# Revit family: Univers-IP30-empty-Surface_mounted-NoHosted-CH-en
name_source: partatom
category: Electrical Equipment
units: mm (PartAtom-declared; Revit-internal decimal feet)

## family parameters
Always vertical = Yes
Cut with Voids When Loaded = No
Panel Configuration = Two Columns, Circuits Across
Part Type = Panelboard
Room Calculation Point = No
Round Connector Dimension = Use Diameter
Shared = No
Work Plane-Based = Yes

## types (20) — shared parameters
Default Elevation = 1219 mm
EF000007 - Colour = EV000202 - White
EF000049 - Depth = 161 mm  [stored 0.528215 ft]
EF000116 - RAL-number = 9010
EF000118 - With mounting plate = No
EF000339 - Type of cover = EV000494 - None
EF001062 - EMC-version = No
EF001088 - Extension possible = No
EF001134 - DIN-rail = No
EF001596 - Material housing = EV000179 - Steel
EF004462 - Type of closure = EV000154 - Other
EF005474 - Degree of protection (IP) = EV006410 - IP30
EF006244 - Transparent cover/door = No
EF006306 - With lock = No
EF015776 - Earthing terminal block = No
EF015777 - Neutral terminal block = No
EF015941 - Signal passing door = No
HG000002 - With door or cover = No
HG000003 - Range = Univers
HG000005 - Thickness = 3 mm  [stored 0.00984252 ft]
HG000006 - Flush mounted = No
HG000009 - Double swing door = No
HG000010 - Asymmetric doors = No
HG000011 - Empty rows from bottom = No
Manufacturer = Hager
Type Comments = Univers
zero-valued in all types: EF000266 - Number of rows, EF002950 - Width in number of modular spacings, HG000001 - Number of columns, HG000007 - Number of empty columns, HG000008 - Number of empty rows

## per-type parameters (varying)
| type | EF000003 - Mounting method | EF000008 - Width | EF000040 - Height | EF000218 - Built-in depth | EF000332 - Built-in height | EF000846 - Built-in width | EF001131 - Internal depth | EF009212 - Cover model | HG000004 - Manufacturer reference | Model |
| Surface mounted IP30 W1050 H1100 D161 0 Modular spacings - FWB74D1 | EV001247 - Surface mounted/recessed mounted | 1050 mm | 1100 mm | 161 mm  [stored 0.528215 ft] | 1100 mm | 1050 mm | 156 mm  [stored 0.511811 ft] | EV009916 - With notch | FWB74D1 | FWB74D1 |
| Surface mounted IP30 W1050 H500 D161 0 Modular spacings - FWB34D1 | EV001247 - Surface mounted/recessed mounted | 1050 mm | 500 mm  [stored 1.64042 ft] | 161 mm  [stored 0.528215 ft] | 500 mm  [stored 1.64042 ft] | 1050 mm | 156 mm  [stored 0.511811 ft] | EV009916 - With notch | FWB34D1 | FWB34D1 |
| Surface mounted IP30 W1050 H650 D161 0 Modular spacings - FWB44D1 | EV001247 - Surface mounted/recessed mounted | 1050 mm | 650 mm  [stored 2.13255 ft] | 161 mm  [stored 0.528215 ft] | 650 mm  [stored 2.13255 ft] | 1050 mm | 160 mm  [stored 0.524934 ft] | EV000116 - Closed | FWB44D1 | FWB44D1 |
| Surface mounted IP30 W1050 H800 D161 0 Modular spacings - FWB54D1 | EV001247 - Surface mounted/recessed mounted | 1050 mm | 800 mm  [stored 2.62467 ft] | 161 mm  [stored 0.528215 ft] | 800 mm  [stored 2.62467 ft] | 1050 mm | 160 mm  [stored 0.524934 ft] | EV009916 - With notch | FWB54D1 | FWB54D1 |
| Surface mounted IP30 W1050 H950 D161 0 Modular spacings - FWB64D1 | EV001247 - Surface mounted/recessed mounted | 1050 mm | 950 mm  [stored 3.1168 ft] | 161 mm  [stored 0.528215 ft] | 950 mm  [stored 3.1168 ft] | 1050 mm | 160 mm  [stored 0.524934 ft] | EV009916 - With notch | FWB64D1 | FWB64D1 |
| Surface mounted IP30 W300 H1100 D161 0 Modular spacings - FWB71D1 | EV001247 - Surface mounted/recessed mounted | 300 mm | 1100 mm | 161 mm  [stored 0.528215 ft] | 1100 mm | 300 mm | 156 mm  [stored 0.511811 ft] | EV009916 - With notch | FWB71D1 | FWB71D1 |
| Surface mounted IP30 W300 H1250 D161 0 Modular spacings - FWB81D1 | EV000384 - Surface mounted (plaster) | 300 mm | 1250 mm  [stored 4.10105 ft] | 0 mm  [stored 0 ft] | 0 mm  [stored 0 ft] | 0 mm  [stored 0 ft] | 160 mm  [stored 0.524934 ft] | EV009916 - With notch | FWB81D1 | FWB81D1 |
| Surface mounted IP30 W300 H500 D161 0 Modular spacings - FWB31D1 | EV001247 - Surface mounted/recessed mounted | 300 mm | 500 mm  [stored 1.64042 ft] | 161 mm  [stored 0.528215 ft] | 500 mm  [stored 1.64042 ft] | 300 mm | 156 mm  [stored 0.511811 ft] | EV009916 - With notch | FWB31D1 | FWB31D1 |
| Surface mounted IP30 W300 H650 D161 0 Modular spacings - FWB41D1 | EV001247 - Surface mounted/recessed mounted | 300 mm | 650 mm  [stored 2.13255 ft] | 161 mm  [stored 0.528215 ft] | 650 mm  [stored 2.13255 ft] | 300 mm | 160 mm  [stored 0.524934 ft] | EV000116 - Closed | FWB41D1 | FWB41D1 |
| Surface mounted IP30 W300 H800 D161 0 Modular spacings - FWB51D1 | EV001247 - Surface mounted/recessed mounted | 300 mm | 800 mm  [stored 2.62467 ft] | 161 mm  [stored 0.528215 ft] | 800 mm  [stored 2.62467 ft] | 300 mm | 156 mm  [stored 0.511811 ft] | EV009916 - With notch | FWB51D1 | FWB51D1 |
| Surface mounted IP30 W300 H950 D161 0 Modular spacings - FWB61D1 | EV001247 - Surface mounted/recessed mounted | 300 mm | 950 mm  [stored 3.1168 ft] | 161 mm  [stored 0.528215 ft] | 950 mm  [stored 3.1168 ft] | 300 mm | 156 mm  [stored 0.511811 ft] | EV009916 - With notch | FWB61D1 | FWB61D1 |
| Surface mounted IP30 W550 H1100 D161 0 Modular spacings - FWB72D1 | EV001247 - Surface mounted/recessed mounted | 550 mm | 1100 mm | 161 mm  [stored 0.528215 ft] | 1100 mm | 550 mm | 156 mm  [stored 0.511811 ft] | EV009916 - With notch | FWB72D1 | FWB72D1 |
| Surface mounted IP30 W550 H500 D161 0 Modular spacings - FWB32D1 | EV001247 - Surface mounted/recessed mounted | 550 mm | 500 mm  [stored 1.64042 ft] | 161 mm  [stored 0.528215 ft] | 500 mm  [stored 1.64042 ft] | 550 mm | 156 mm  [stored 0.511811 ft] | EV009916 - With notch | FWB32D1 | FWB32D1 |
| Surface mounted IP30 W550 H650 D161 0 Modular spacings - FWB42D1 | EV001247 - Surface mounted/recessed mounted | 550 mm | 650 mm  [stored 2.13255 ft] | 161 mm  [stored 0.528215 ft] | 650 mm  [stored 2.13255 ft] | 550 mm | 160 mm  [stored 0.524934 ft] | EV000116 - Closed | FWB42D1 | FWB42D1 |
| Surface mounted IP30 W550 H800 D161 0 Modular spacings - FWB52D1 | EV001247 - Surface mounted/recessed mounted | 550 mm | 800 mm  [stored 2.62467 ft] | 161 mm  [stored 0.528215 ft] | 800 mm  [stored 2.62467 ft] | 550 mm | 156 mm  [stored 0.511811 ft] | EV009916 - With notch | FWB52D1 | FWB52D1 |
| Surface mounted IP30 W550 H950 D161 0 Modular spacings - FWB62D1 | EV001247 - Surface mounted/recessed mounted | 550 mm | 950 mm  [stored 3.1168 ft] | 161 mm  [stored 0.528215 ft] | 950 mm  [stored 3.1168 ft] | 550 mm | 156 mm  [stored 0.511811 ft] | EV009916 - With notch | FWB62D1 | FWB62D1 |
| Surface mounted IP30 W800 H500 D161 0 Modular spacings - FWB33D1 | EV001247 - Surface mounted/recessed mounted | 800 mm  [stored 2.62467 ft] | 500 mm  [stored 1.64042 ft] | 161 mm  [stored 0.528215 ft] | 500 mm  [stored 1.64042 ft] | 800 mm  [stored 2.62467 ft] | 160 mm  [stored 0.524934 ft] | EV000116 - Closed | FWB33D1 | FWB33D1 |
| Surface mounted IP30 W800 H650 D161 0 Modular spacings - FWB43D1 | EV001247 - Surface mounted/recessed mounted | 800 mm  [stored 2.62467 ft] | 650 mm  [stored 2.13255 ft] | 161 mm  [stored 0.528215 ft] | 650 mm  [stored 2.13255 ft] | 800 mm  [stored 2.62467 ft] | 160 mm  [stored 0.524934 ft] | EV000116 - Closed | FWB43D1 | FWB43D1 |
| Surface mounted IP30 W800 H800 D161 0 Modular spacings - FWB53D1 | EV001247 - Surface mounted/recessed mounted | 800 mm  [stored 2.62467 ft] | 800 mm  [stored 2.62467 ft] | 161 mm  [stored 0.528215 ft] | 800 mm  [stored 2.62467 ft] | 800 mm  [stored 2.62467 ft] | 160 mm  [stored 0.524934 ft] | EV000116 - Closed | FWB53D1 | FWB53D1 |
| Surface mounted IP30 W800 H950 D161 0 Modular spacings - FWB63D1 | EV001247 - Surface mounted/recessed mounted | 800 mm  [stored 2.62467 ft] | 950 mm  [stored 3.1168 ft] | 161 mm  [stored 0.528215 ft] | 950 mm  [stored 3.1168 ft] | 800 mm  [stored 2.62467 ft] | 160 mm  [stored 0.524934 ft] | EV009916 - With notch | FWB63D1 | FWB63D1 |

note: [stored X ft] marks values corroborated as IEEE doubles in the binary element streams (Revit-internal decimal feet)

## geometry (parser evidence)
native form markers: Sweep x16
no freeform markers — native parametric forms only
